# Revit family: 201_OKA-_+VAL
name_source: partatom
category: Air Terminals
units: mm (PartAtom-declared; Revit-internal decimal feet)

## family parameters
Always vertical = Yes
Cut with Voids When Loaded = No
Part Type = Normal
Room Calculation Point = Yes
Round Connector Dimension = Use Diameter
Shared = No
Work Plane-Based = No

## types (4) — shared parameters
A3 = 5 mm  [stored 0.0164042 ft]
CAT0 = Yes
CL_Location_5000 = 5000 mm
Description = Air diffuser with plenum sound attenuator
H1 = 2 mm  [stored 0.00656168 ft]
H1__ve = -2 mm  [stored -0.00656168 ft]
L_ARR = 400 mm
Manufacturer = Climecon
QmdConnectorList = 201;D
URL = www.climecon.fi
W_ARR = 400 mm
XRefLineVPlnId = 7453
YRefLineVPlnId = 7456
magiPartTypeId = 201
magiProductFamilyId = OKA-*+VAL
zero-valued in all types: CLBTZ, H_ARR, MC_Default_elevation

## per-type parameters (varying)
| type | A | A2 | AA1 | AA2 | B1 | B2 | CLD | D | E2 | E3 | E4 | E4__ve | E6 | E8 | K | K1 |
| OKA-100+VAL | 205 mm  [stored 0.672572 ft] | 103 mm | 190 mm  [stored 0.62336 ft] | 185 mm  [stored 0.606955 ft] | 100 mm  [stored 0.328084 ft] | 95 mm  [stored 0.31168 ft] | 100 mm  [stored 0.328084 ft] | 100 mm | 146 mm  [stored 0.479003 ft] | 148 mm  [stored 0.485564 ft] | 35 mm  [stored 0.114829 ft] | -35 mm  [stored -0.114829 ft] | 45 mm  [stored 0.147638 ft] | 58 mm  [stored 0.190289 ft] | 100 mm  [stored 0.328084 ft] | 95 mm  [stored 0.31168 ft] |
| OKA-200+VAL | 320 mm | 160 mm  [stored 0.524934 ft] | 290 mm | 285 mm | 150 mm  [stored 0.492126 ft] | 145 mm  [stored 0.475722 ft] | 200 mm  [stored 0.656168 ft] | 200 mm | 246 mm | 248 mm | 55 mm  [stored 0.180446 ft] | -55 mm  [stored -0.180446 ft] | 65 mm  [stored 0.213255 ft] | 108 mm  [stored 0.354331 ft] | 150 mm  [stored 0.492126 ft] | 145 mm  [stored 0.475722 ft] |
| OKA-160+VAL | 255 mm | 128 mm | 250 mm | 245 mm | 130 mm  [stored 0.426509 ft] | 125 mm  [stored 0.410105 ft] | 160 mm  [stored 0.524934 ft] | 160 mm | 206 mm  [stored 0.675853 ft] | 208 mm  [stored 0.682415 ft] | 45 mm  [stored 0.147638 ft] | -45 mm  [stored -0.147638 ft] | 55 mm  [stored 0.180446 ft] | 88 mm  [stored 0.288714 ft] | 130 mm  [stored 0.426509 ft] | 125 mm  [stored 0.410105 ft] |
| OKA-125+VAL | 205 mm  [stored 0.672572 ft] | 103 mm | 215 mm | 210 mm  [stored 0.688976 ft] | 115 mm  [stored 0.377297 ft] | 110 mm  [stored 0.360892 ft] | 125 mm  [stored 0.410105 ft] | 125 mm | 171 mm  [stored 0.561024 ft] | 173 mm  [stored 0.567585 ft] | 44 mm  [stored 0.144357 ft] | -44 mm  [stored -0.144357 ft] | 54 mm  [stored 0.177165 ft] | 73 mm  [stored 0.239501 ft] | 115 mm  [stored 0.377297 ft] | 110 mm  [stored 0.360892 ft] |

note: column(s) folded — value = type name in every type: magiProductCode, magiProductId

note: [stored X ft] marks values corroborated as IEEE doubles in the binary element streams (Revit-internal decimal feet)

## geometry (parser evidence)
native form markers: Sweep x1
no freeform markers — native parametric forms only
